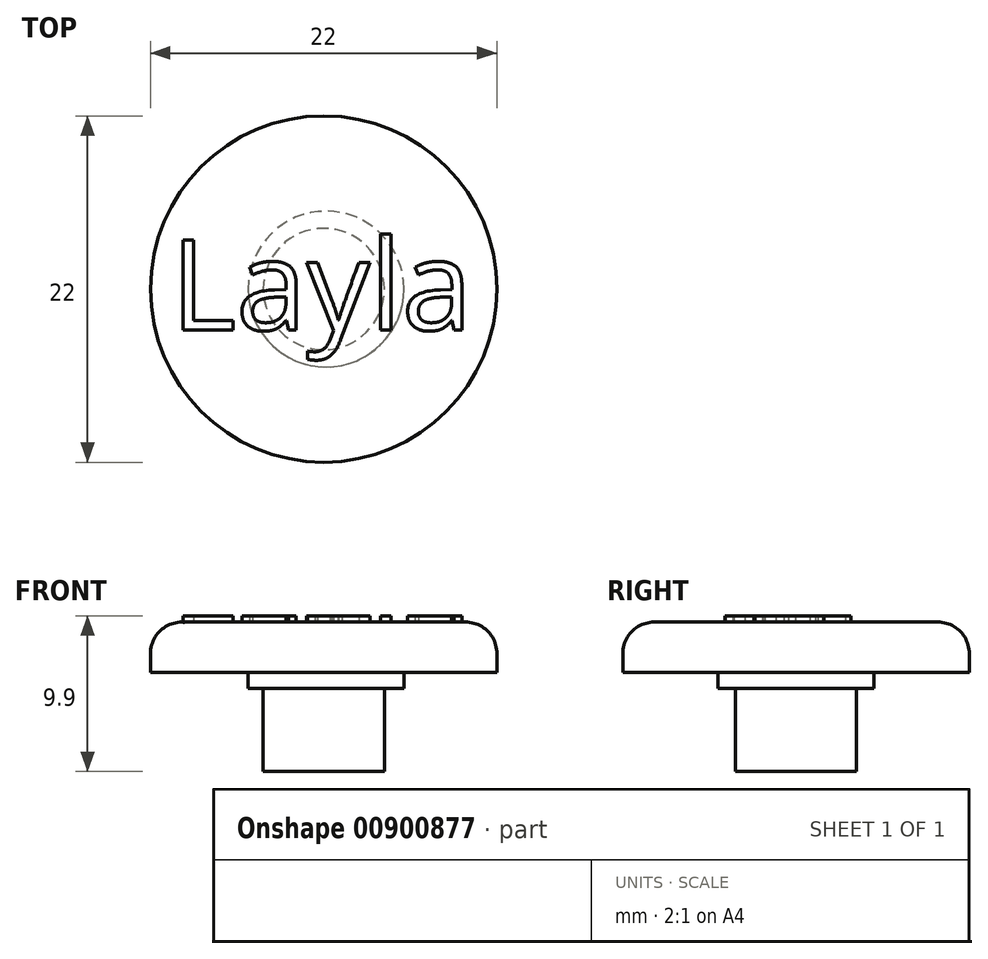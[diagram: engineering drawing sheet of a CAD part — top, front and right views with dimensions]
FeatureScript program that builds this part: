
annotation { "Feature Type Name" : "Feature", "Feature Type Description" : "" }
export const myFeature = defineFeature(function(context is Context, id is Id, definition is map)
    precondition{}
    {
        {
            var Q0;
            Q0=qCreatedBy(makeId("Top.planeOp"),FACE);
            var sketch = newSketch(context, id + "F0", { "sketchPlane" : qUnion([Q0])});
            skCircle(sketch, "E0", {"center": v(0, 0) * mm, "radius": 11 * mm});
            skSolve(sketch);
        }
        {
            var Q0;
            Q0 = qSketchRegion(id + "F0", true);
            extrude(context, id + "F1", {"entities" : qUnion([Q0]), "depth" : 3.2 * mm, "offsetDistance" : 25 * mm});
        }
        {
            var Q0;
            Q0=makeQuery(id+"F1.opExtrude","CAP_FACE",FACE,{"disambiguationData":[OSD([sQuery(id+"F0.wireOp",EDGE,"E0")])],"isStart":true});
            var sketch = newSketch(context, id + "F2", { "sketchPlane" : qUnion([Q0])});
            skCircle(sketch, "E1", {"center": v(0, 0) * mm, "radius": 3.85 * mm});
            skCircle(sketch, "E2", {"center": v(0.15, 0) * mm, "radius": 4.95 * mm});
            skSolve(sketch);
        }
        {
            var Q0;
            Q0=makeQuery(id+"F2.imprint","IMPRINT",FACE,{"disambiguationData":[TD([[makeQuery(id+"F2.imprint","IMPRINT",EDGE,{"derivedFrom":sQuery(id+"F2.wireOp",EDGE,"E1")}),1.0]])]});
            extrude(context, id + "F3", {"entities" : qUnion([Q0]), "operationType" : NewBodyOperationType.ADD, "depth" : 6.3 * mm, "offsetDistance" : 25 * mm});
        }
        {
            var Q0;
            Q0=makeQuery(id+"F2.imprint","IMPRINT",FACE,{"disambiguationData":[TD([[makeQuery(id+"F2.imprint","IMPRINT",EDGE,{"derivedFrom":sQuery(id+"F2.wireOp",EDGE,"E1")}),-1.0]])]});
            extrude(context, id + "F4", {"entities" : qUnion([Q0]), "operationType" : NewBodyOperationType.ADD, "depth" : 1 * mm, "offsetDistance" : 25 * mm});
        }
        {
            var Q0;
            Q0=makeQuery(id+"F1.opExtrude","CAP_FACE",FACE,{"disambiguationData":[OSD([sQuery(id+"F0.wireOp",EDGE,"E0")])],"isStart":false});
            var sketch = newSketch(context, id + "F5", { "sketchPlane" : qUnion([Q0])});
            skText(sketch, "E3", { "text": "Layla", "fontName": "OpenSans-Regular.ttf"});
            const initialGuessF5  = {"E3": [-0.00972, -0.0026, 1, 0, 0.00577]};
            skSetInitialGuess(sketch, initialGuessF5);
            skSolve(sketch);
        }
        {
            var Q0;
            Q0 = qSketchRegion(id + "F5", true);
            extrude(context, id + "F6", {"entities" : qUnion([Q0]), "operationType" : NewBodyOperationType.ADD, "depth" : 0.4 * mm, "offsetDistance" : 25 * mm});
        }
        {
            var Q0;
            Q0=makeQuery(id+"F1.opExtrude","CAP_EDGE",EDGE,{"disambiguationData":[OSD([sQuery(id+"F0.wireOp",EDGE,"E0")])],"isStart":false});
            fillet(context, id + "F7", {"entities" : qUnion([Q0]), "radius" : 2 * mm, "tangentPropagation" : true, "allowEdgeOverflow" : false});
        }
    });
